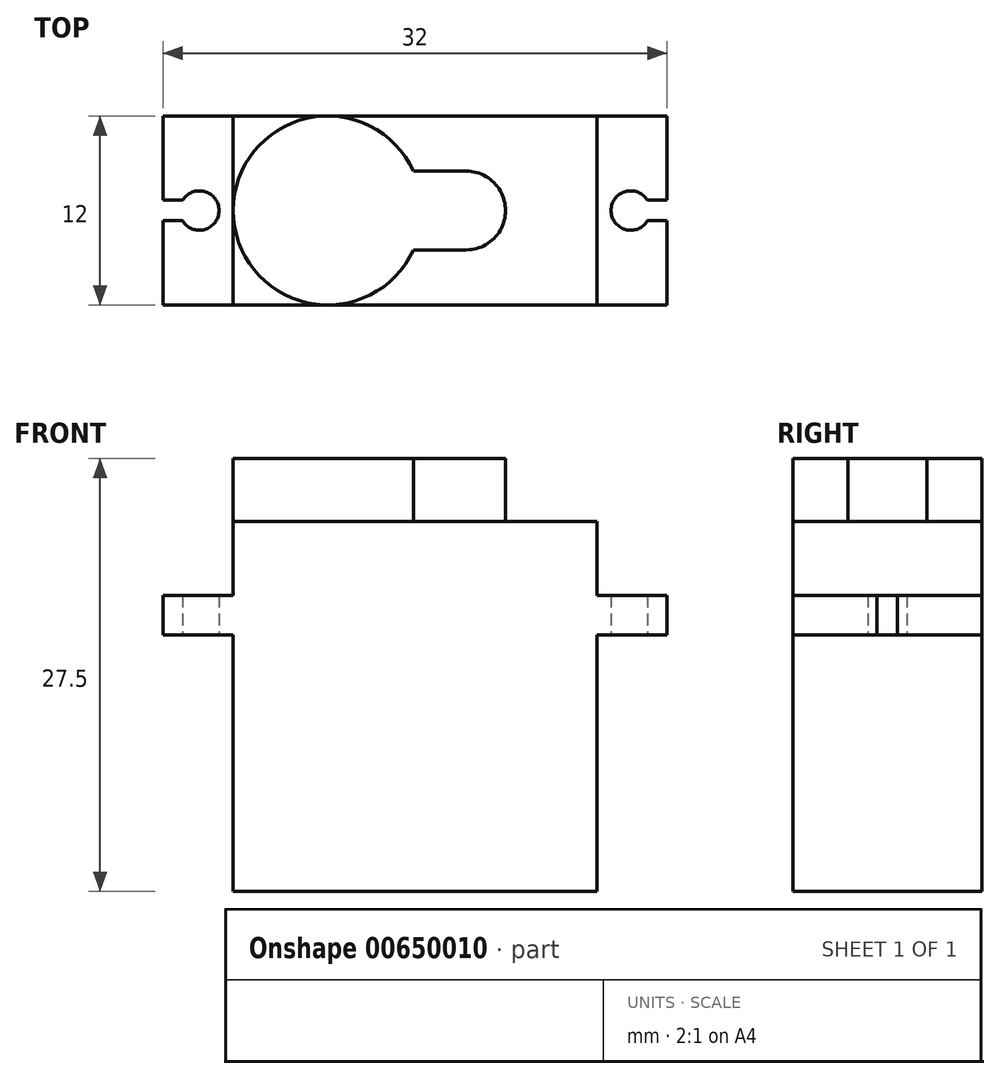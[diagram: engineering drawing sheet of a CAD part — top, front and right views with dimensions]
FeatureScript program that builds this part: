
annotation { "Feature Type Name" : "Feature", "Feature Type Description" : "" }
export const myFeature = defineFeature(function(context is Context, id is Id, definition is map)
    precondition{}
    {
        {
            assignVariable(context, id + "F0", {"name" : "servo_body_height", "anyValue" : 23.5});
        }
        {
            assignVariable(context, id + "F1", {"name" : "servo_motor_height", "anyValue" : 4});
        }
        {
            assignVariable(context, id + "F2", {"name" : "servo_tab_thickness", "anyValue" : 2.5});
        }
        {
            assignVariable(context, id + "F3", {"name" : "servo_tab_vertical_offset", "anyValue" : 4.7});
        }
        {
            var Q0;
            Q0=qCreatedBy(makeId("Top.planeOp"),FACE);
            var sketch = newSketch(context, id + "F4", { "sketchPlane" : qUnion([Q0])});
            skLineSegment(sketch, "E0.bottom", {"start": v(11.55, -6) * mm, "end": v(-11.55, -6) * mm});
            skLineSegment(sketch, "E0.top", {"start": v(11.55, 6) * mm, "end": v(-11.55, 6) * mm});
            skLineSegment(sketch, "E0.left", {"start": v(11.55, -6) * mm, "end": v(11.55, 6) * mm});
            skLineSegment(sketch, "E0.right", {"start": v(-11.55, -6) * mm, "end": v(-11.55, 6) * mm});
            skPoint(sketch, "E0.middle", {"position": v(0, 0) * mm});
            skLineSegment(sketch, "E1.bottom", {"start": v(16, -6) * mm, "end": v(-16, -6) * mm});
            skLineSegment(sketch, "E1.top", {"start": v(16, 6) * mm, "end": v(-16, 6) * mm});
            skLineSegment(sketch, "E1.left", {"start": v(16, -6) * mm, "end": v(16, 6) * mm});
            skLineSegment(sketch, "E1.right", {"start": v(-16, -6) * mm, "end": v(-16, 6) * mm});
            skLineSegment(sketch, "E2", {"start": v(-16, 0) * mm, "end": v(-13.7, 0) * mm, "construction": true});
            skLineSegment(sketch, "E3", {"start": v(16, 0) * mm, "end": v(13.7, 0) * mm});
            skCircle(sketch, "E4", {"center": v(-13.7, 0) * mm, "radius": 1.25 * mm});
            skCircle(sketch, "E5", {"center": v(13.7, 0) * mm, "radius": 1.25 * mm});
            skLineSegment(sketch, "E6", {"start": v(-11.55, 0) * mm, "end": v(-5.55, 0) * mm, "construction": true});
            skCircle(sketch, "E7", {"center": v(-5.55, 0) * mm, "radius": 6 * mm});
            skLineSegment(sketch, "E8", {"start": v(-5.55, 0) * mm, "end": v(3.25, 0) * mm, "construction": true});
            skCircle(sketch, "E9", {"center": v(3.25, 0) * mm, "radius": 2.5 * mm});
            skLineSegment(sketch, "E10.bottom", {"start": v(3.25, 2.5) * mm, "end": v(-3, 2.5) * mm});
            skLineSegment(sketch, "E10.top", {"start": v(3.25, -2.5) * mm, "end": v(-3, -2.5) * mm});
            skLineSegment(sketch, "E10.left", {"start": v(3.25, 2.5) * mm, "end": v(3.25, -2.5) * mm});
            skLineSegment(sketch, "E10.right", {"start": v(-3, 2.5) * mm, "end": v(-3, -2.5) * mm});
            skLineSegment(sketch, "E11.bottom", {"start": v(14.18, -0.65) * mm, "end": v(17.82, -0.65) * mm});
            skLineSegment(sketch, "E11.top", {"start": v(14.18, 0.65) * mm, "end": v(17.82, 0.65) * mm});
            skLineSegment(sketch, "E11.left", {"start": v(14.18, -0.65) * mm, "end": v(14.18, 0.65) * mm});
            skLineSegment(sketch, "E11.right", {"start": v(17.82, -0.65) * mm, "end": v(17.82, 0.65) * mm});
            skPoint(sketch, "E11.middle", {"position": v(16, 0) * mm});
            skLineSegment(sketch, "E12.bottom", {"start": v(-14.12, -0.65) * mm, "end": v(-17.88, -0.65) * mm});
            skLineSegment(sketch, "E12.top", {"start": v(-14.12, 0.65) * mm, "end": v(-17.88, 0.65) * mm});
            skLineSegment(sketch, "E12.left", {"start": v(-14.12, -0.65) * mm, "end": v(-14.12, 0.65) * mm});
            skLineSegment(sketch, "E12.right", {"start": v(-17.88, -0.65) * mm, "end": v(-17.88, 0.65) * mm});
            skPoint(sketch, "E12.middle", {"position": v(-16, 0) * mm});
            skSolve(sketch);
        }
        {
            var Q0;
            {var subQ0=sQuery(id+"F4.wireOp",EDGE,"E0.left");Q0=makeQuery(id+"F4.imprint","IMPRINT",FACE,{"disambiguationData":[TD([[makeQuery(id+"F4.imprint","IMPRINT",EDGE,{"derivedFrom":subQ0}),1.0]])]});}
            var Q1;
            {var subQ0=sQuery(id+"F4.wireOp",EDGE,"E7");var subQ1=makeQuery(id+"F4.imprint","INTERSECT",VERTEX,{"derivedFrom":[sQuery(id+"F4.wireOp",EDGE,"E1.top"),subQ0]});Q1=makeQuery(id+"F4.imprint","IMPRINT",FACE,{"disambiguationData":[TD([[makeQuery(id+"F4.imprint","IMPRINT",EDGE,{"disambiguationData":[TD([[subQ1,-1.0]])],"derivedFrom":subQ0}),1.0]])]});}
            var Q2;
            {var subQ0=sQuery(id+"F4.wireOp",EDGE,"E1.top");var subQ1=sQuery(id+"F4.wireOp",EDGE,"E0.right");var subQ2=makeQuery(id+"F4.imprint","INTERSECT",VERTEX,{"derivedFrom":[subQ1,subQ0]});Q2=makeQuery(id+"F4.imprint","IMPRINT",FACE,{"disambiguationData":[TD([[makeQuery(id+"F4.imprint","IMPRINT",EDGE,{"disambiguationData":[TD([[subQ2,1.0]])],"derivedFrom":subQ1}),-1.0]])]});}
            var Q3;
            {var subQ0=sQuery(id+"F4.wireOp",EDGE,"E1.bottom");var subQ1=sQuery(id+"F4.wireOp",EDGE,"E0.right");var subQ2=makeQuery(id+"F4.imprint","INTERSECT",VERTEX,{"derivedFrom":[subQ1,subQ0]});Q3=makeQuery(id+"F4.imprint","IMPRINT",FACE,{"disambiguationData":[TD([[makeQuery(id+"F4.imprint","IMPRINT",EDGE,{"disambiguationData":[TD([[subQ2,-1.0]])],"derivedFrom":subQ1}),-1.0]])]});}
            var Q4;
            {var subQ0=sQuery(id+"F4.wireOp",EDGE,"E10.left");Q4=makeQuery(id+"F4.imprint","IMPRINT",FACE,{"disambiguationData":[TD([[makeQuery(id+"F4.imprint","IMPRINT",EDGE,{"derivedFrom":subQ0}),1.0]])]});}
            var Q5;
            {var subQ0=sQuery(id+"F4.wireOp",EDGE,"E10.left");Q5=makeQuery(id+"F4.imprint","IMPRINT",FACE,{"disambiguationData":[TD([[makeQuery(id+"F4.imprint","IMPRINT",EDGE,{"derivedFrom":subQ0}),-1.0]])]});}
            var Q6;
            {var subQ5=sQuery(id+"F4.wireOp",EDGE,"E10.right");Q6=makeQuery(id+"F4.imprint","IMPRINT",FACE,{"disambiguationData":[TD([[makeQuery(id+"F4.imprint","IMPRINT",EDGE,{"derivedFrom":subQ5}),1.0]])]});}
            var Q7;
            {var subQ0=sQuery(id+"F4.wireOp",EDGE,"E10.bottom");var subQ1=sQuery(id+"F4.wireOp",EDGE,"E7");var subQ2=makeQuery(id+"F4.imprint","INTERSECT",VERTEX,{"derivedFrom":[subQ1,subQ0]});Q7=makeQuery(id+"F4.imprint","IMPRINT",FACE,{"disambiguationData":[TD([[makeQuery(id+"F4.imprint","IMPRINT",EDGE,{"disambiguationData":[TD([[subQ2,1.0]])],"derivedFrom":subQ1}),-1.0]])]});}
            extrude(context, id + "F5", {"entities" : qUnion([Q0, Q1, Q2, Q3, Q4, Q5, Q6, Q7]), "depth" : (getVariable(context, 'servo_body_height')) * mm, "offsetDistance" : 25 * mm});
        }
        {
            var Q0;
            {var subQ4=sQuery(id+"F4.wireOp",EDGE,"E0.left");Q0=makeQuery(id+"F4.imprint","IMPRINT",FACE,{"disambiguationData":[TD([[makeQuery(id+"F4.imprint","IMPRINT",EDGE,{"derivedFrom":subQ4}),-1.0]])]});}
            var Q1;
            {var subQ3=sQuery(id+"F4.wireOp",EDGE,"E1.right");Q1=makeQuery(id+"F4.imprint","IMPRINT",FACE,{"disambiguationData":[TD([[makeQuery(id+"F4.imprint","IMPRINT",EDGE,{"derivedFrom":subQ3}),-1.0]])]});}
            extrude(context, id + "F6", {"entities" : qUnion([Q0, Q1]), "operationType" : NewBodyOperationType.ADD, "depth" : (getVariable(context, 'servo_body_height') - getVariable(context, 'servo_tab_vertical_offset')) * mm, "offsetDistance" : 25 * mm, "hasSecondDirection" : true, "secondDirectionOppositeDirection" : false, "secondDirectionDepth" : ((getVariable(context, 'servo_body_height') - getVariable(context, 'servo_tab_vertical_offset')) - getVariable(context, 'servo_tab_thickness')) * mm});
        }
        {
            var Q0;
            {var subQ0=sQuery(id+"F4.wireOp",EDGE,"E7");var subQ1=makeQuery(id+"F4.imprint","INTERSECT",VERTEX,{"derivedFrom":[sQuery(id+"F4.wireOp",EDGE,"E1.top"),subQ0]});Q0=makeQuery(id+"F4.imprint","IMPRINT",FACE,{"disambiguationData":[TD([[makeQuery(id+"F4.imprint","IMPRINT",EDGE,{"disambiguationData":[TD([[subQ1,-1.0]])],"derivedFrom":subQ0}),1.0]])]});}
            var Q1;
            {var subQ5=sQuery(id+"F4.wireOp",EDGE,"E10.right");Q1=makeQuery(id+"F4.imprint","IMPRINT",FACE,{"disambiguationData":[TD([[makeQuery(id+"F4.imprint","IMPRINT",EDGE,{"derivedFrom":subQ5}),1.0]])]});}
            var Q2;
            {var subQ0=sQuery(id+"F4.wireOp",EDGE,"E10.bottom");var subQ1=sQuery(id+"F4.wireOp",EDGE,"E7");var subQ2=makeQuery(id+"F4.imprint","INTERSECT",VERTEX,{"derivedFrom":[subQ1,subQ0]});Q2=makeQuery(id+"F4.imprint","IMPRINT",FACE,{"disambiguationData":[TD([[makeQuery(id+"F4.imprint","IMPRINT",EDGE,{"disambiguationData":[TD([[subQ2,1.0]])],"derivedFrom":subQ1}),-1.0]])]});}
            var Q3;
            {var subQ0=sQuery(id+"F4.wireOp",EDGE,"E10.left");Q3=makeQuery(id+"F4.imprint","IMPRINT",FACE,{"disambiguationData":[TD([[makeQuery(id+"F4.imprint","IMPRINT",EDGE,{"derivedFrom":subQ0}),-1.0]])]});}
            var Q4;
            {var subQ0=sQuery(id+"F4.wireOp",EDGE,"E10.left");Q4=makeQuery(id+"F4.imprint","IMPRINT",FACE,{"disambiguationData":[TD([[makeQuery(id+"F4.imprint","IMPRINT",EDGE,{"derivedFrom":subQ0}),1.0]])]});}
            extrude(context, id + "F7", {"entities" : qUnion([Q0, Q1, Q2, Q3, Q4]), "operationType" : NewBodyOperationType.ADD, "depth" : (getVariable(context, 'servo_body_height') + getVariable(context, 'servo_motor_height')) * mm, "offsetDistance" : 25 * mm});
        }
    });
